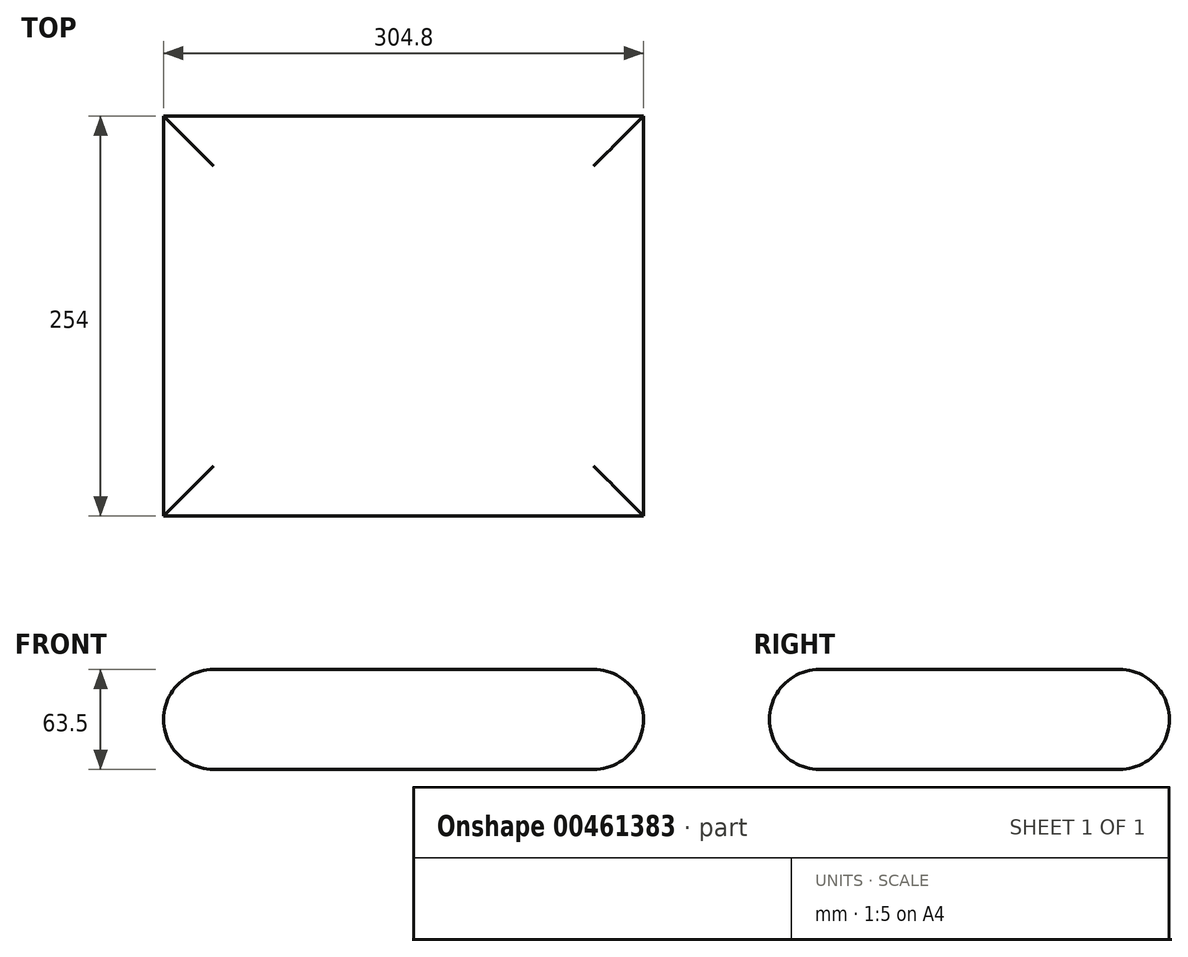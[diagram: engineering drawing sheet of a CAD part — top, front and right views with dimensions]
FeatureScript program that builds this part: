
annotation { "Feature Type Name" : "Feature", "Feature Type Description" : "" }
export const myFeature = defineFeature(function(context is Context, id is Id, definition is map)
    precondition{}
    {
        {
            var Q0;
            Q0=qCreatedBy(makeId("Top.planeOp"),FACE);
            var sketch = newSketch(context, id + "F0", { "sketchPlane" : qUnion([Q0])});
            skLineSegment(sketch, "E0.bottom", {"start": v(152.4, 127) * mm, "end": v(-152.4, 127) * mm});
            skLineSegment(sketch, "E0.top", {"start": v(152.4, -127) * mm, "end": v(-152.4, -127) * mm});
            skLineSegment(sketch, "E0.left", {"start": v(152.4, 127) * mm, "end": v(152.4, -127) * mm});
            skLineSegment(sketch, "E0.right", {"start": v(-152.4, 127) * mm, "end": v(-152.4, -127) * mm});
            skPoint(sketch, "E0.middle", {"position": v(0, 0) * mm});
            skSolve(sketch);
        }
        {
            var Q0;
            Q0 = qSketchRegion(id + "F0", true);
            extrude(context, id + "F1", {"entities" : qUnion([Q0]), "depth" : 63.5 * mm});
        }
        {
            var Q0;
            Q0=makeQuery(id+"F1.opExtrude","CAP_FACE",FACE,{"disambiguationData":[OSD([sQuery(id+"F0.wireOp",EDGE,"E0.bottom"),sQuery(id+"F0.wireOp",EDGE,"E0.top"),sQuery(id+"F0.wireOp",EDGE,"E0.left"),sQuery(id+"F0.wireOp",EDGE,"E0.right")])],"isStart":false});
            fillet(context, id + "F2", {"entities" : qUnion([Q0]), "radius" : 31.75 * mm, "tangentPropagation" : true, "allowEdgeOverflow" : false});
        }
        {
            var Q0;
            Q0=makeQuery(id+"F1.opExtrude","CAP_FACE",FACE,{"disambiguationData":[OSD([sQuery(id+"F0.wireOp",EDGE,"E0.bottom"),sQuery(id+"F0.wireOp",EDGE,"E0.top"),sQuery(id+"F0.wireOp",EDGE,"E0.left"),sQuery(id+"F0.wireOp",EDGE,"E0.right")])],"isStart":true});
            fillet(context, id + "F3", {"entities" : qUnion([Q0]), "radius" : 31.75 * mm, "tangentPropagation" : true, "allowEdgeOverflow" : false});
        }
    });
